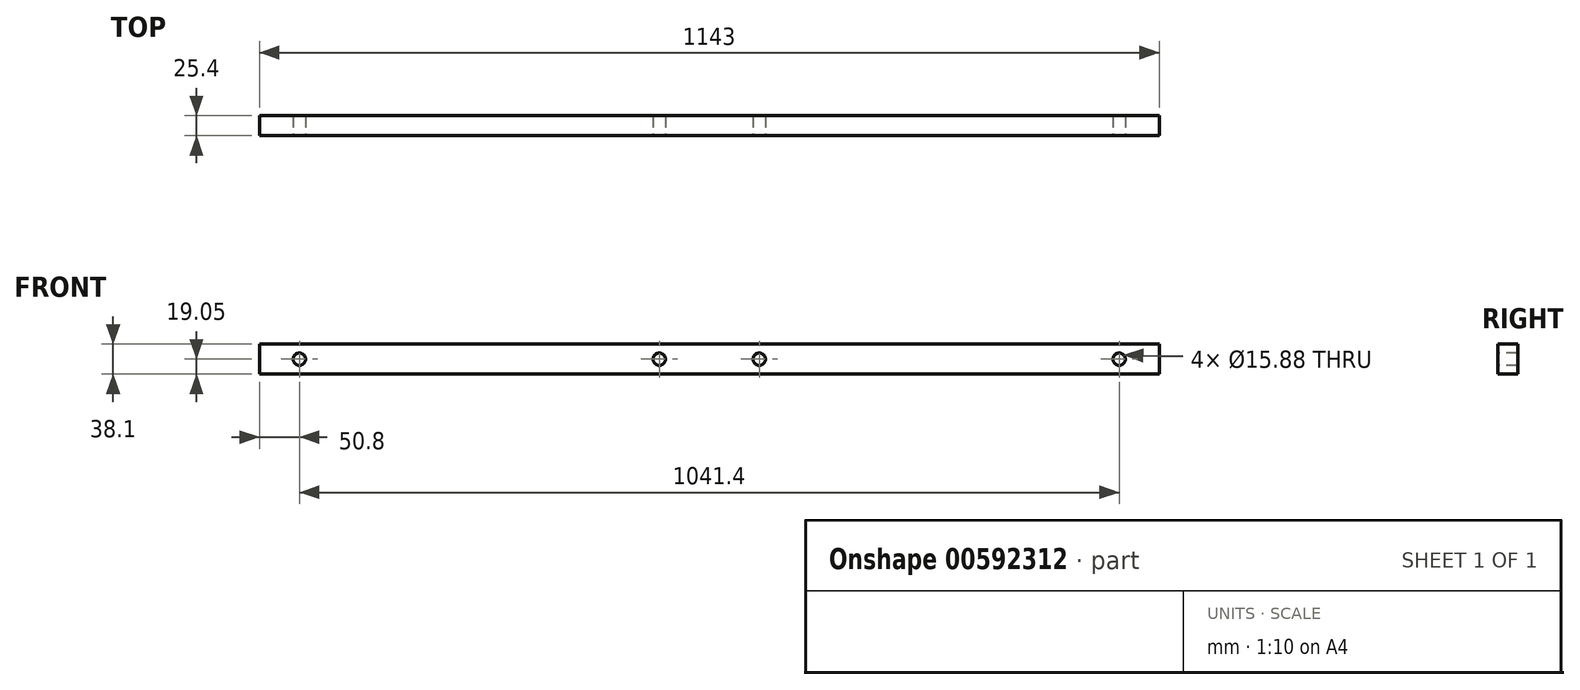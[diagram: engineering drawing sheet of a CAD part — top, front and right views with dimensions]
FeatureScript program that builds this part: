
annotation { "Feature Type Name" : "Feature", "Feature Type Description" : "" }
export const myFeature = defineFeature(function(context is Context, id is Id, definition is map)
    precondition{}
    {
        {
            var Q0;
            Q0=qCreatedBy(makeId("Front.planeOp"),FACE);
            var sketch = newSketch(context, id + "F0", { "sketchPlane" : qUnion([Q0])});
            skLineSegment(sketch, "E0.bottom", {"start": v(0, 0) * mm, "end": v(1143, 0) * mm});
            skLineSegment(sketch, "E0.top", {"start": v(0, 38.1) * mm, "end": v(1143, 38.1) * mm});
            skLineSegment(sketch, "E0.left", {"start": v(0, 0) * mm, "end": v(0, 38.1) * mm});
            skLineSegment(sketch, "E0.right", {"start": v(1143, 0) * mm, "end": v(1143, 38.1) * mm});
            skSolve(sketch);
        }
        {
            var Q0;
            Q0=makeQuery(id+"F0.imprint","IMPRINT",FACE,{"disambiguationData":[TD([[makeQuery(id+"F0.imprint","IMPRINT",EDGE,{"derivedFrom":sQuery(id+"F0.wireOp",EDGE,"E0.bottom")}),1.0]])]});
            extrude(context, id + "F1", {"entities" : qUnion([Q0]), "depth" : 25.4 * mm, "offsetDistance" : 25.4 * mm});
        }
        {
            var Q0;
            Q0=makeQuery(id+"F1.opExtrude","CAP_FACE",FACE,{"disambiguationData":[OSD([sQuery(id+"F0.wireOp",EDGE,"E0.bottom"),sQuery(id+"F0.wireOp",EDGE,"E0.top"),sQuery(id+"F0.wireOp",EDGE,"E0.left"),sQuery(id+"F0.wireOp",EDGE,"E0.right")])],"isStart":false});
            var sketch = newSketch(context, id + "F2", { "sketchPlane" : qUnion([Q0])});
            skCircle(sketch, "E1", {"center": v(50.8, 19.05) * mm, "radius": 6.35 * mm});
            skCircle(sketch, "E2", {"center": v(1092.2, 19.05) * mm, "radius": 6.35 * mm});
            skCircle(sketch, "E3", {"center": v(508, 19.05) * mm, "radius": 6.35 * mm});
            skCircle(sketch, "E4", {"center": v(635, 19.05) * mm, "radius": 6.35 * mm});
            skSolve(sketch);
        }
        {
            var Q0;
            Q0=sQuery(id+"F2.wireOp",VERTEX,"E1.center");
            var Q1;
            Q1=sQuery(id+"F2.wireOp",VERTEX,"E3.center");
            var Q2;
            Q2=sQuery(id+"F2.wireOp",VERTEX,"E4.center");
            var Q3;
            Q3=sQuery(id+"F2.wireOp",VERTEX,"E2.center");
            var Q4;
            Q4=makeQuery(id+"F1.opExtrude","SWEPT_BODY",BODY,{"disambiguationData":[OSD([sQuery(id+"F0.wireOp",EDGE,"E0.bottom"),sQuery(id+"F0.wireOp",EDGE,"E0.top"),sQuery(id+"F0.wireOp",EDGE,"E0.left"),sQuery(id+"F0.wireOp",EDGE,"E0.right")])]});
            hole(context, id + "F3", {"style" : HoleStyle.SIMPLE, "endStyle" : HoleEndStyle.THROUGH, "holeDiameter" : 15.88 * mm, "majorDiameter" : 6.35 * mm, "isTappedThrough" : true, "tappedDepth" : 12.7 * mm, "tapClearance" : 3, "locations" : qUnion([Q0, Q1, Q2, Q3]), "scope" : qUnion([Q4])});
        }
    });
